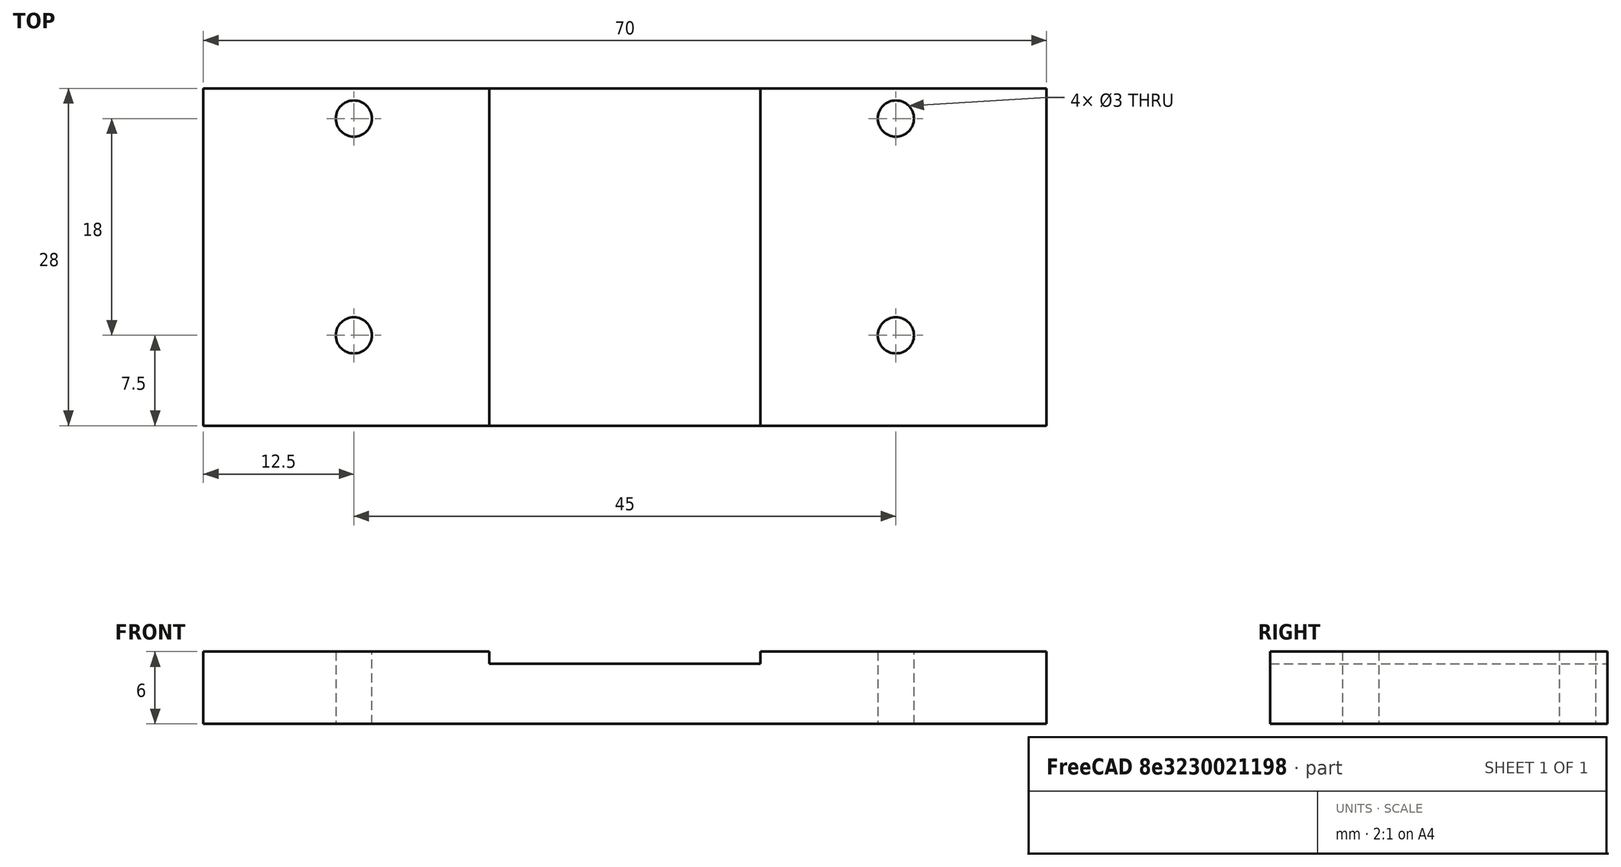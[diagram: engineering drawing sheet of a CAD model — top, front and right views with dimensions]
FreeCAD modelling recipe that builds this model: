
FCSTD DOCUMENT  (FreeCAD 0.18R16146 (Git))
Label: linefollower
License: All rights reserved
LicenseURL: http://en.wikipedia.org/wiki/All_rights_reserved
objects: Sketcher::SketchObject×2, PartDesign::Pad×1, PartDesign::Pocket×1, PartDesign::Body×1, Mesh::Feature×1
note: 7 computed .brp shape members not serialized (recipe doc carries the construction recipe); baked Part::Feature solids carry a one-line shape summary decoded from their .brp

FEATURE [Sketcher::SketchObject] Sketch
  MapMode = 5
  Support = -> [XY_Plane]
  sketch-geometry (8):
    g0: LineSegment StartX=0 StartY=0 StartZ=0 EndX=70 EndY=0 EndZ=0
    g1: LineSegment StartX=70 StartY=0 StartZ=0 EndX=70 EndY=28 EndZ=0
    g2: LineSegment StartX=70 StartY=28 StartZ=0 EndX=0 EndY=28 EndZ=0
    g3: LineSegment StartX=0 StartY=28 StartZ=0 EndX=0 EndY=0 EndZ=0
    g4: Circle CenterX=12.5 CenterY=25.5 CenterZ=0 NormalX=0 NormalY=0 NormalZ=1 AngleXU=0 Radius=1.5
    g5: Circle CenterX=57.5 CenterY=25.5 CenterZ=0 NormalX=0 NormalY=0 NormalZ=1 AngleXU=0 Radius=1.5
    g6: Circle CenterX=57.5 CenterY=7.5 CenterZ=0 NormalX=0 NormalY=0 NormalZ=1 AngleXU=0 Radius=1.5
    g7: Circle CenterX=12.5 CenterY=7.5 CenterZ=0 NormalX=0 NormalY=0 NormalZ=1 AngleXU=0 Radius=1.5
  constraints (23):
    c: Coincident(g0,g1)
    c: Coincident(g1,g2)
    c: Coincident(g2,g3)
    c: Coincident(g3,g0)
    c: Horizontal(g0)
    c: Horizontal(g2)
    c: Vertical(g1)
    c: Vertical(g3)
    c: Coincident(g0,g-1)
    c: DistanceX(g0,g0) = 70
    c: DistanceY(g3,g3) = 28
    c: Radius(g4) = 1.5
    c: Equal(g4,g5) = 1.5
    c: Equal(g4,g6) = 1.5
    c: Equal(g4,g7) = 1.5
    c: Vertical(g4,g7)
    c: Vertical(g6,g5)
    c: Horizontal(g6,g7)
    c: Horizontal(g4,g5)
    c: DistanceY(g6,g5) = 18
    c: DistanceX(g4,g5) = 45
    c: DistanceX(g0,g7) = 12.5
    c: DistanceY(g0,g7) = 7.5
FEATURE [PartDesign::Pad] Pad
  Length = 6
  Length2 = 100
  Profile = -> Sketch
  Type = 0
FEATURE [Sketcher::SketchObject] Sketch001
  MapMode = 5
  Placement = pos=(0,0,6) rot=(0,0,1;0rad)
  Support = -> [Pad]
  sketch-geometry (4):
    g0: LineSegment StartX=23.75 StartY=0 StartZ=0 EndX=46.25 EndY=0 EndZ=0
    g1: LineSegment StartX=46.25 StartY=0 StartZ=0 EndX=46.25 EndY=28 EndZ=0
    g2: LineSegment StartX=46.25 StartY=28 StartZ=0 EndX=23.75 EndY=28 EndZ=0
    g3: LineSegment StartX=23.75 StartY=28 StartZ=0 EndX=23.75 EndY=0 EndZ=0
  constraints (12):
    c: Coincident(g0,g1)
    c: Coincident(g1,g2)
    c: Coincident(g2,g3)
    c: Coincident(g3,g0)
    c: Horizontal(g0)
    c: Horizontal(g2)
    c: Vertical(g1)
    c: Vertical(g3)
    c: DistanceX(g0,g0) = 22.5
    c: DistanceX(g-1,g0) = 23.75
    c: Horizontal(g-1,g0)
    c: DistanceY(g3,g3) = 28
FEATURE [PartDesign::Pocket] Pocket
  BaseFeature = -> Pad
  Length = 1
  Length2 = 100
  Profile = -> Sketch001
  Type = 0
FEATURE [PartDesign::Body] Body
  Group = -> [Sketch,Pad,Sketch001,Pocket]
  Origin = -> Origin
  Tip = -> Pocket
FEATURE [Mesh::Feature] Mesh  label="Body (Meshed)"
